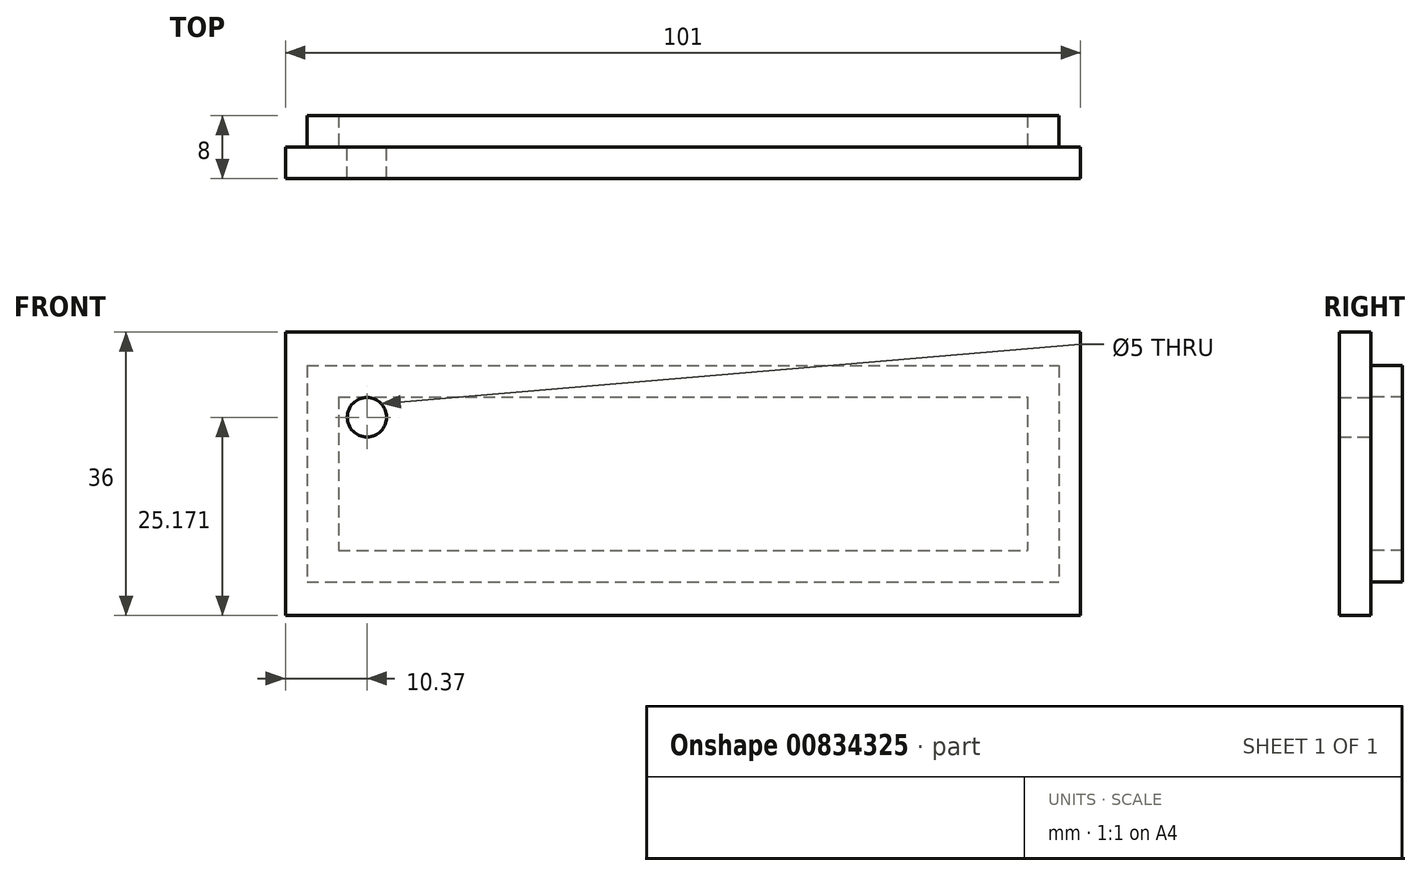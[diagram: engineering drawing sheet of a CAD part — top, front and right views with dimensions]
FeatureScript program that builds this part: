
annotation { "Feature Type Name" : "Feature", "Feature Type Description" : "" }
export const myFeature = defineFeature(function(context is Context, id is Id, definition is map)
    precondition{}
    {
        {
            var Q0;
            Q0=qCreatedBy(makeId("Front.planeOp"),FACE);
            var sketch = newSketch(context, id + "F0", { "sketchPlane" : qUnion([Q0])});
            skLineSegment(sketch, "E0.bottom", {"start": v(50.5, -18) * mm, "end": v(-50.5, -18) * mm});
            skLineSegment(sketch, "E0.top", {"start": v(50.5, 18) * mm, "end": v(-50.5, 18) * mm});
            skLineSegment(sketch, "E0.left", {"start": v(50.5, -18) * mm, "end": v(50.5, 18) * mm});
            skLineSegment(sketch, "E0.right", {"start": v(-50.5, -18) * mm, "end": v(-50.5, 18) * mm});
            skPoint(sketch, "E0.middle", {"position": v(0, 0) * mm});
            skLineSegment(sketch, "E1.bottom", {"start": v(47.75, -13.75) * mm, "end": v(-47.75, -13.75) * mm});
            skLineSegment(sketch, "E1.top", {"start": v(47.75, 13.75) * mm, "end": v(-47.75, 13.75) * mm});
            skLineSegment(sketch, "E1.left", {"start": v(47.75, -13.75) * mm, "end": v(47.75, 13.75) * mm});
            skLineSegment(sketch, "E1.right", {"start": v(-47.75, -13.75) * mm, "end": v(-47.75, 13.75) * mm});
            skLineSegment(sketch, "E2.0", {"start": v(43.75, 9.75) * mm, "end": v(-43.75, 9.75) * mm});
            skLineSegment(sketch, "E2.1", {"start": v(43.75, -9.75) * mm, "end": v(43.75, 9.75) * mm});
            skLineSegment(sketch, "E2.2", {"start": v(43.75, -9.75) * mm, "end": v(-43.75, -9.75) * mm});
            skLineSegment(sketch, "E2.3", {"start": v(-43.75, -9.75) * mm, "end": v(-43.75, 9.75) * mm});
            skSolve(sketch);
        }
        {
            var Q0;
            Q0=makeQuery(id+"F0.imprint","IMPRINT",FACE,{"disambiguationData":[TD([[makeQuery(id+"F0.imprint","IMPRINT",EDGE,{"derivedFrom":sQuery(id+"F0.wireOp",EDGE,"E1.bottom")}),-1.0]])]});
            var Q1;
            Q1=makeQuery(id+"F0.imprint","IMPRINT",FACE,{"disambiguationData":[TD([[makeQuery(id+"F0.imprint","IMPRINT",EDGE,{"derivedFrom":sQuery(id+"F0.wireOp",EDGE,"E0.bottom")}),-1.0]])]});
            var Q2;
            Q2=makeQuery(id+"F0.imprint","IMPRINT",FACE,{"disambiguationData":[TD([[makeQuery(id+"F0.imprint","IMPRINT",EDGE,{"derivedFrom":sQuery(id+"F0.wireOp",EDGE,"E2.0")}),1.0]])]});
            extrude(context, id + "F1", {"entities" : qUnion([Q0, Q1, Q2]), "depth" : 4 * mm, "offsetDistance" : 25 * mm});
        }
        {
            var Q0;
            Q0=qCreatedBy(makeId("Front.planeOp"),FACE);
            var sketch = newSketch(context, id + "F2", { "sketchPlane" : qUnion([Q0])});
            skLineSegment(sketch, "E3.bottom", {"start": v(-47.75, 13.75) * mm, "end": v(47.75, 13.75) * mm});
            skLineSegment(sketch, "E3.top", {"start": v(-47.75, -13.75) * mm, "end": v(47.75, -13.75) * mm});
            skLineSegment(sketch, "E3.left", {"start": v(-47.75, 13.75) * mm, "end": v(-47.75, -13.75) * mm});
            skLineSegment(sketch, "E3.right", {"start": v(47.75, 13.75) * mm, "end": v(47.75, -13.75) * mm});
            skPoint(sketch, "E3.middle", {"position": v(0, 0) * mm});
            skLineSegment(sketch, "E4.0", {"start": v(-43.75, -9.75) * mm, "end": v(43.75, -9.75) * mm});
            skLineSegment(sketch, "E4.1", {"start": v(-43.75, 9.75) * mm, "end": v(-43.75, -9.75) * mm});
            skLineSegment(sketch, "E4.2", {"start": v(-43.75, 9.75) * mm, "end": v(43.75, 9.75) * mm});
            skLineSegment(sketch, "E4.3", {"start": v(43.75, 9.75) * mm, "end": v(43.75, -9.75) * mm});
            skSolve(sketch);
        }
        {
            var Q0;
            Q0=makeQuery(id+"F1.opExtrude","CAP_FACE",FACE,{"disambiguationData":[OSD([sQuery(id+"F0.wireOp",EDGE,"E0.bottom"),sQuery(id+"F0.wireOp",EDGE,"E0.top"),sQuery(id+"F0.wireOp",EDGE,"E0.left"),sQuery(id+"F0.wireOp",EDGE,"E0.right")])],"isStart":false});
            var Q1;
            Q1=makeQuery(id+"F2.imprint","IMPRINT",FACE,{"disambiguationData":[TD([[makeQuery(id+"F2.imprint","IMPRINT",EDGE,{"derivedFrom":sQuery(id+"F2.wireOp",EDGE,"E3.bottom")}),-1.0]])]});
            extrude(context, id + "F3", {"entities" : qUnion([Q0, Q1]), "operationType" : NewBodyOperationType.ADD, "oppositeDirection" : true, "depth" : 4 * mm, "offsetDistance" : 25 * mm});
        }
        {
            var Q0;
            Q0=qCreatedBy(makeId("Front.planeOp"),FACE);
            var sketch = newSketch(context, id + "F4", { "sketchPlane" : qUnion([Q0])});
            skPoint(sketch, "E5", {"position": v(-40.13, 7.17) * mm});
            skSolve(sketch);
        }
        {
            var Q0;
            Q0=sQuery(id+"F4.wireOp",VERTEX,"E5");
            var Q1;
            Q1=makeQuery(id+"F1.opExtrude","SWEPT_BODY",BODY,{"disambiguationData":[OSD([sQuery(id+"F0.wireOp",EDGE,"E0.bottom"),sQuery(id+"F0.wireOp",EDGE,"E0.top"),sQuery(id+"F0.wireOp",EDGE,"E0.left"),sQuery(id+"F0.wireOp",EDGE,"E0.right")])]});
            hole(context, id + "F5", {"style" : HoleStyle.SIMPLE, "endStyle" : HoleEndStyle.BLIND, "oppositeDirection" : true, "holeDiameter" : 5 * mm, "majorDiameter" : 5 * mm, "holeDepth" : 6 * mm, "isTappedThrough" : true, "tappedDepth" : 12 * mm, "tapClearance" : 3, "startFromSketch" : true, "locations" : qUnion([Q0]), "scope" : qUnion([Q1])});
        }
    });
